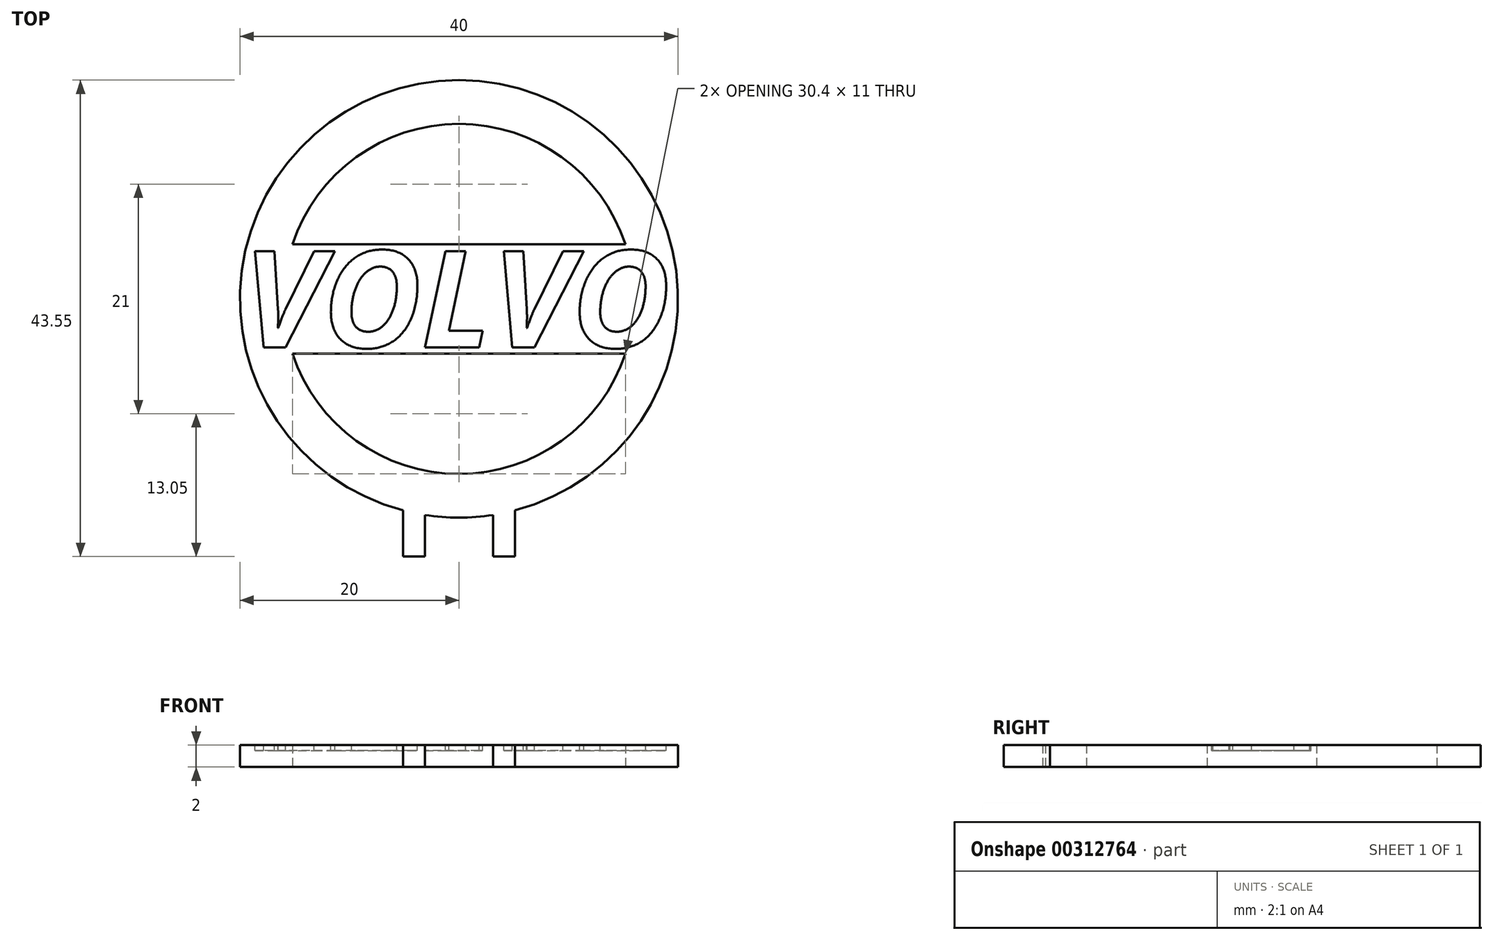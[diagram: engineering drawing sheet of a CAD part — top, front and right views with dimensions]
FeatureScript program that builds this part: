
annotation { "Feature Type Name" : "Feature", "Feature Type Description" : "" }
export const myFeature = defineFeature(function(context is Context, id is Id, definition is map)
    precondition{}
    {
        {
            var Q0;
            Q0=qCreatedBy(makeId("Top.planeOp"),FACE);
            var sketch = newSketch(context, id + "F0", { "sketchPlane" : qUnion([Q0])});
            skCircle(sketch, "E0", {"center": v(0, 0) * mm, "radius": 20 * mm});
            skCircle(sketch, "E1", {"center": v(0, 0) * mm, "radius": 16 * mm});
            skLineSegment(sketch, "E2", {"start": v(0, 0) * mm, "end": v(16, 0) * mm});
            skLineSegment(sketch, "E3", {"start": v(0, 0) * mm, "end": v(-16, 0) * mm});
            skLineSegment(sketch, "E4.0", {"start": v(0, -5) * mm, "end": v(15.2, -5) * mm});
            skLineSegment(sketch, "E4.1", {"start": v(0, -5) * mm, "end": v(-15.2, -5) * mm});
            skLineSegment(sketch, "E5.0", {"start": v(0, 5) * mm, "end": v(-15.2, 5) * mm});
            skLineSegment(sketch, "E5.1", {"start": v(0, 5) * mm, "end": v(15.2, 5) * mm});
            skLineSegment(sketch, "E6", {"start": v(-3.1, -19.76) * mm, "end": v(-3.1, -23.55) * mm});
            skLineSegment(sketch, "E7", {"start": v(3.1, -23.55) * mm, "end": v(3.1, -19.76) * mm});
            skLineSegment(sketch, "E8", {"start": v(-5.1, -19.34) * mm, "end": v(-5.1, -23.55) * mm});
            skLineSegment(sketch, "E9", {"start": v(-5.1, -23.55) * mm, "end": v(-3.1, -23.55) * mm});
            skLineSegment(sketch, "E10", {"start": v(3.1, -23.55) * mm, "end": v(5.1, -23.55) * mm});
            skLineSegment(sketch, "E11", {"start": v(5.1, -23.55) * mm, "end": v(5.1, -19.34) * mm});
            skSolve(sketch);
        }
        {
            var Q0;
            Q0 = qSketchRegion(id + "F0", true);
            var Q1;
            {var subQ0=sQuery(id+"F0.wireOp",EDGE,"E2");Q1=makeQuery(id+"F0.imprint","IMPRINT",FACE,{"disambiguationData":[TD([[makeQuery(id+"F0.imprint","IMPRINT",EDGE,{"derivedFrom":subQ0}),1.0]])]});}
            var Q2;
            {var subQ1=sQuery(id+"F0.wireOp",EDGE,"E2");Q2=makeQuery(id+"F0.imprint","IMPRINT",FACE,{"disambiguationData":[TD([[makeQuery(id+"F0.imprint","IMPRINT",EDGE,{"derivedFrom":subQ1}),-1.0]])]});}
            extrude(context, id + "F1", {"entities" : qUnion([Q0, Q1, Q2]), "depth" : 2 * mm});
        }
        {
            var Q0;
            Q0=makeQuery(id+"F1.opExtrude","CAP_FACE",FACE,{"disambiguationData":[OSD([sQuery(id+"F0.wireOp",EDGE,"E0"),sQuery(id+"F0.wireOp",EDGE,"E1"),sQuery(id+"F0.wireOp",EDGE,"E4.0"),sQuery(id+"F0.wireOp",EDGE,"E4.1"),sQuery(id+"F0.wireOp",EDGE,"E5.0"),sQuery(id+"F0.wireOp",EDGE,"E5.1")])],"isStart":false});
            var sketch = newSketch(context, id + "F2", { "sketchPlane" : qUnion([Q0])});
            skText(sketch, "E12", { "text": "VOLVO\n", "fontName": "OpenSans-BoldItalic.ttf"});
            const initialGuessF2  = {"E12": [-0.01973, -0.00445, 1, 0, 0.0089]};
            skSetInitialGuess(sketch, initialGuessF2);
            skSolve(sketch);
        }
        {
            var Q0;
            Q0=makeQuery(id+"F2.imprint","IMPRINT",FACE,{"disambiguationData":[TD([[makeQuery(id+"F2.imprint","IMPRINT",EDGE,{"derivedFrom":sQuery(id+"F2.wireOp",EDGE,"E12.sketch_text.stroke-11")}),-1.0]])]});
            var Q1;
            Q1=makeQuery(id+"F2.imprint","IMPRINT",FACE,{"disambiguationData":[TD([[makeQuery(id+"F2.imprint","IMPRINT",EDGE,{"derivedFrom":sQuery(id+"F2.wireOp",EDGE,"E12.sketch_text.stroke-31")}),-1.0]])]});
            var Q2;
            Q2=makeQuery(id+"F2.imprint","IMPRINT",FACE,{"disambiguationData":[TD([[makeQuery(id+"F2.imprint","IMPRINT",EDGE,{"derivedFrom":sQuery(id+"F2.wireOp",EDGE,"E12.sketch_text.stroke-0")}),-1.0]])]});
            var Q3;
            Q3=makeQuery(id+"F2.imprint","IMPRINT",FACE,{"disambiguationData":[TD([[makeQuery(id+"F2.imprint","IMPRINT",EDGE,{"derivedFrom":sQuery(id+"F2.wireOp",EDGE,"E12.sketch_text.stroke-37")}),-1.0]])]});
            var Q4;
            Q4=makeQuery(id+"F2.imprint","IMPRINT",FACE,{"disambiguationData":[TD([[makeQuery(id+"F2.imprint","IMPRINT",EDGE,{"derivedFrom":sQuery(id+"F2.wireOp",EDGE,"E12.sketch_text.stroke-48")}),-1.0]])]});
            extrude(context, id + "F3", {"entities" : qUnion([Q0, Q1, Q2, Q3, Q4]), "operationType" : NewBodyOperationType.REMOVE, "oppositeDirection" : true, "depth" : 0.5 * mm});
        }
    });
